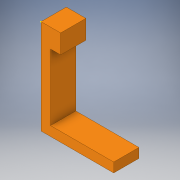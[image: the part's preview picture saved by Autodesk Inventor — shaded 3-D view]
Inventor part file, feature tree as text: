
AUTODESK INVENTOR PART (.ipt)
format: ipt  version: 2017 (Build 210142000, 142)  size: 111,616 bytes
history: native  units: in
note: dims shown in document units (in); Inventor stores cm internally (conversion verified against a paired STEP export)
features: sketch x4, extrude x3
ambient origin geometry x8: Origin, YZ Plane, XZ Plane, XY Plane, X Axis, Y Axis, Z Axis, Center Point
bodies: Solid1 (feature_tree)
feature tree (7):
  extrude  "Extrusion1"  Depth=3.75in
  extrude  "Extrusion2"  Depth=0.75in
  extrude  "Extrusion3"  Depth=1.0in
  sketch  "Sketch6"  dims[d8=0.375in d9=2.5in d10=0.0in]
  sketch  "Sketch1"  dims[d0=0.375in d1=3.75in]
  sketch  "Sketch2"  dims[d2=1.0in d3=0.0in d4=0.75in]
  sketch  "Sketch3"  dims[d5=0.4in d6=0.0in d7=1.0in]
